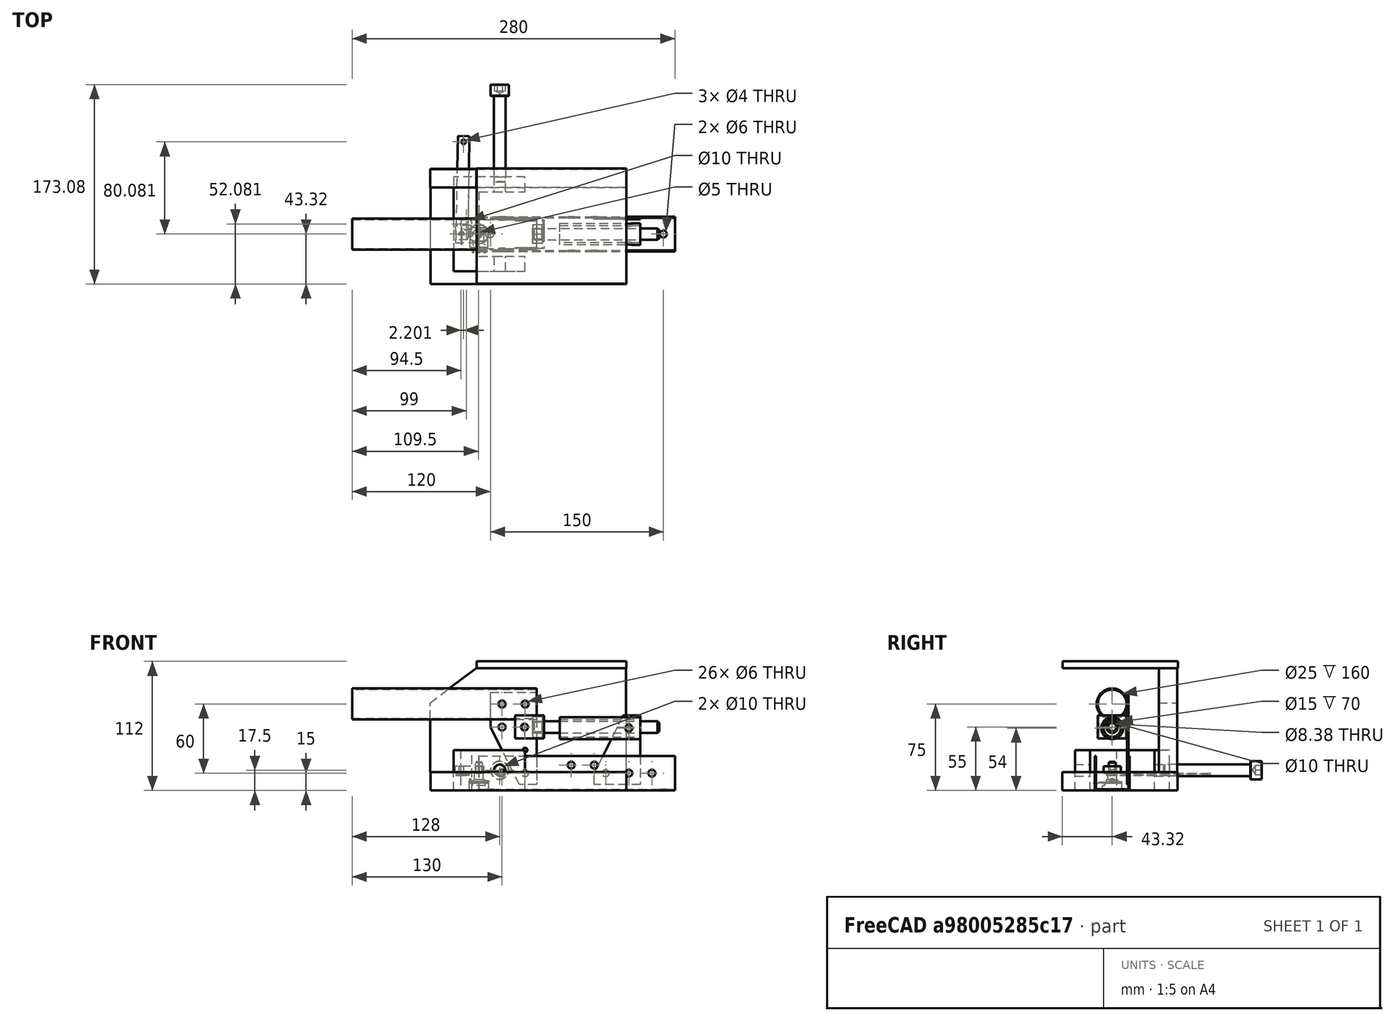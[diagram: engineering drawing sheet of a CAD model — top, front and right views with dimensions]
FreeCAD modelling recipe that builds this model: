
FCSTD DOCUMENT  (FreeCAD 0.19R24267 +99 (Git))
Label: HandBrake
License: All rights reserved
LicenseURL: http://en.wikipedia.org/wiki/All_rights_reserved
objects: TechDraw::DrawViewDimension×36, Sketcher::SketchObject×20, PartDesign::Pad×12, PartDesign::Body×12, TechDraw::DrawProjGroupItem×12, TechDraw::DrawProjGroup×9, PartDesign::Pocket×8, App::Part×7, Part::FeaturePython×3, Part::Mirroring×3, PartDesign::Thickness×2, PartDesign::Chamfer×2, Part::Feature×2, TechDraw::DrawSVGTemplate×2, TechDraw::DrawPage×2, App::DocumentObjectGroup×1
note: 88 computed .brp shape members not serialized (recipe doc carries the construction recipe); baked Part::Feature solids carry a one-line shape summary decoded from their .brp

FEATURE [Sketcher::SketchObject] Sketch
  FullyConstrained = false
  MapMode = 5
  Placement = pos=(0,0,0) rot=(0.57735,0.57735,0.57735;2.0944rad)
  Support = -> [YZ_Plane001]
  sketch-geometry (11):
    g0: LineSegment StartX=-15 StartY=0 StartZ=0 EndX=15 EndY=0 EndZ=0
    g1: LineSegment StartX=15 StartY=0 StartZ=0 EndX=15 EndY=30 EndZ=0
    g2: LineSegment StartX=15 StartY=30 StartZ=0 EndX=-15 EndY=30 EndZ=0
    g3: LineSegment StartX=-15 StartY=30 StartZ=0 EndX=-15 EndY=0 EndZ=0
    g4: LineSegment StartX=-14 StartY=1 StartZ=0 EndX=14 EndY=1 EndZ=0
    g5: LineSegment StartX=14 StartY=1 StartZ=0 EndX=14 EndY=30 EndZ=0
    g6: LineSegment StartX=14 StartY=30 StartZ=0 EndX=-14 EndY=30 EndZ=0
    g7: LineSegment StartX=-14 StartY=30 StartZ=0 EndX=-14 EndY=1 EndZ=0
    g8: LineSegment StartX=-15 StartY=30 StartZ=0 EndX=-14 EndY=30 EndZ=0
    g9: LineSegment StartX=14 StartY=30 StartZ=0 EndX=15 EndY=30 EndZ=0
    g10: LineSegment StartX=5.44004 StartY=1 StartZ=0 EndX=5.44004 EndY=0 EndZ=0
  constraints (30):
    c: Coincident(g0,g1)
    c: Coincident(g1,g2)
    c: Coincident(g2,g3)
    c: Coincident(g3,g0)
    c: Horizontal(g0)
    c: Horizontal(g2)
    c: Vertical(g1)
    c: Vertical(g3)
    c: Coincident(g4,g5)
    c: Coincident(g5,g6)
    c: Coincident(g6,g7)
    c: Coincident(g7,g4)
    c: Horizontal(g4)
    c: Horizontal(g6)
    c: Vertical(g5)
    c: Vertical(g7)
    c: PointOnObject(g5,g2)
    c: Coincident(g8,g3)
    c: Coincident(g8,g7)
    c: Coincident(g9,g5)
    c: Coincident(g9,g1)
    c: DistanceY(g1,g1) = 30
    c: DistanceX(g0,g0) = 30
    c: Equal(g8,g9)
    c: DistanceX(g8,g8) = 1
    c: PointOnObject(g10,g4)
    c: PointOnObject(g10,g0)
    c: Equal(g10,g9)
    c: Perpendicular(g0,g10)
    c: Symmetric(g0,g0,g-1)
FEATURE [PartDesign::Pad] Pad
  Direction = (1,1,1)
  Length = 170
  Length2 = 100
  Placement = pos=(0,0,0) rot=(0.57735,0.57735,0.57735;2.0944rad)
  Profile = -> Sketch
  Type = 0
FEATURE [Sketcher::SketchObject] Sketch001
  FullyConstrained = true
  MapMode = 5
  Support = -> [XY_Plane002]
  sketch-geometry (1):
    g0: Circle CenterX=0 CenterY=0 CenterZ=0 NormalX=0 NormalY=0 NormalZ=1 AngleXU=0 Radius=12.5
  constraints (2):
    c: Coincident(g0,g-1)
    c: Diameter(g0) = 25
FEATURE [PartDesign::Pad] Pad001
  Direction = (1,1,1)
  Length = 160
  Length2 = 100
  Profile = -> Sketch001
  Type = 0
FEATURE [PartDesign::Thickness] Thickness
  Base = -> Pad001 [Face3,Face2]
  BaseFeature = -> Pad001
  Intersection = false
  Join = 1
  Mode = 1
  SupportTransform = false
  Value = 1
FEATURE [Sketcher::SketchObject] Sketch002
  ExternalGeometry = -> [Thickness]
  FullyConstrained = true
  MapMode = 5
  Placement = pos=(0,0,0) rot=(1,0,0;1.5708rad)
  Support = -> [XZ_Plane002]
  sketch-geometry (2):
    g0: Circle CenterX=0 CenterY=10 CenterZ=0 NormalX=0 NormalY=0 NormalZ=1 AngleXU=0 Radius=3
    g1: Circle CenterX=0 CenterY=30 CenterZ=0 NormalX=0 NormalY=0 NormalZ=1 AngleXU=0 Radius=3
  constraints (6):
    c: PointOnObject(g0,g-2)
    c: Diameter(g0) = 6
    c: PointOnObject(g1,g-2)
    c: Equal(g1,g0)
    c: Distance(g1,g0) = 20
    c: DistanceY(g-1,g0) = 10
FEATURE [PartDesign::Pocket] Pocket
  BaseFeature = -> Thickness
  Length = 5
  Length2 = 100
  Midplane = true
  Profile = -> Sketch002
  Type = 1
FEATURE [PartDesign::Body] Body001  label="Рычаг"
  Group = -> [Sketch001,Pad001,Thickness,Sketch002,Pocket]
  Origin = -> Origin002
  Placement = pos=(50,0,75) rot=(0,-1,0;1.5708rad)
  Tip = -> Pocket
FEATURE [Sketcher::SketchObject] Sketch003
  ExternalGeometry = -> [Pad]
  FullyConstrained = false
  MapMode = 5
  Placement = pos=(-6.6e-15,-15,3.3e-15) rot=(-0.57735,-0.57735,0.57735;4.18879rad)
  Support = -> [Pad]
  sketch-geometry (7):
    g0: Circle CenterX=-15 CenterY=20 CenterZ=0 NormalX=0 NormalY=0 NormalZ=1 AngleXU=0 Radius=3
    g1: Circle CenterX=-15 CenterY=150 CenterZ=0 NormalX=0 NormalY=0 NormalZ=1 AngleXU=0 Radius=3
    g2: LineSegment StartX=-15 StartY=170 StartZ=0 EndX=-15 EndY=0 EndZ=0
    g3: Circle CenterX=-15 CenterY=130 CenterZ=0 NormalX=0 NormalY=0 NormalZ=1 AngleXU=0 Radius=3
    g4: LineSegment StartX=-22 StartY=170 StartZ=0 EndX=-22 EndY=0 EndZ=0
    g5: Circle CenterX=-22 CenterY=100 CenterZ=0 NormalX=0 NormalY=0 NormalZ=1 AngleXU=0 Radius=3
    g6: Circle CenterX=-22 CenterY=80 CenterZ=0 NormalX=0 NormalY=0 NormalZ=1 AngleXU=0 Radius=3
  constraints (23):
    c: Equal(g1,g0)
    c: Diameter(g0) = 6
    c: PointOnObject(g2,g-4)
    c: Vertical(g2)
    c: Distance(g-4) = 30
    c: Distance(g2,g-5) = 15
    c: PointOnObject(g1,g2)
    c: PointOnObject(g0,g2)
    c: Distance(g0,g2) = 20
    c: Distance(g1,g2) = 20
    c: PointOnObject(g3,g2)
    c: Equal(g3,g1)
    c: Distance(g3,g1) = 20
    c: PointOnObject(g4,g-4)
    c: Vertical(g4)
    c: DistanceX(g-4,g4) = 8
    c: PointOnObject(g5,g4)
    c: Diameter(g5) = 6
    c: DistanceY(g4,g5) = 100
    c: PointOnObject(g6,g4)
    c: Equal(g6,g5)
    c: DistanceY(g6,g5) = 20
    c: PointOnObject(g4,g-1)
FEATURE [PartDesign::Pocket] Pocket001
  BaseFeature = -> Pad
  Length = 5
  Length2 = 100
  Placement = pos=(0,0,0) rot=(0.57735,0.57735,0.57735;2.0944rad)
  Profile = -> Sketch003
  Type = 1
FEATURE [Sketcher::SketchObject] Sketch004
  FullyConstrained = true
  MapMode = 5
  Placement = pos=(0,0,0) rot=(1,0,0;1.5708rad)
  Support = -> [XZ_Plane004]
  sketch-geometry (15):
    g0: LineSegment StartX=-20 StartY=40 StartZ=0 EndX=20 EndY=40 EndZ=0
    g1: LineSegment StartX=20 StartY=40 StartZ=0 EndX=20 EndY=-40 EndZ=0
    g2: LineSegment StartX=20 StartY=-40 StartZ=0 EndX=-20 EndY=-40 EndZ=0
    g3: LineSegment StartX=-20 StartY=-40 StartZ=0 EndX=-20 EndY=40 EndZ=0
    g4: Circle CenterX=-10 CenterY=30 CenterZ=0 NormalX=0 NormalY=0 NormalZ=1 AngleXU=0 Radius=3
    g5: Circle CenterX=10 CenterY=30 CenterZ=0 NormalX=0 NormalY=0 NormalZ=1 AngleXU=0 Radius=3
    g6: LineSegment StartX=-10 StartY=30 StartZ=0 EndX=10 EndY=30 EndZ=0
    g7: LineSegment StartX=10 StartY=30 StartZ=0 EndX=10 EndY=-30 EndZ=0
    g8: LineSegment StartX=10 StartY=-30 StartZ=0 EndX=-10 EndY=-30 EndZ=0
    g9: LineSegment StartX=-10 StartY=-30 StartZ=0 EndX=-10 EndY=30 EndZ=0
    g10: Circle CenterX=10 CenterY=-30 CenterZ=0 NormalX=0 NormalY=0 NormalZ=1 AngleXU=0 Radius=3
    g11: Circle CenterX=-10 CenterY=-30 CenterZ=0 NormalX=0 NormalY=0 NormalZ=1 AngleXU=0 Radius=3
    g12: Circle CenterX=-10 CenterY=10 CenterZ=0 NormalX=0 NormalY=0 NormalZ=1 AngleXU=0 Radius=3
    g13: Circle CenterX=10 CenterY=10 CenterZ=0 NormalX=0 NormalY=0 NormalZ=1 AngleXU=0 Radius=3
    g14: Circle CenterX=10 CenterY=-10 CenterZ=0 NormalX=0 NormalY=0 NormalZ=1 AngleXU=0 Radius=2
  constraints (40):
    c: Coincident(g0,g1)
    c: Coincident(g1,g2)
    c: Coincident(g2,g3)
    c: Coincident(g3,g0)
    c: Horizontal(g0)
    c: Horizontal(g2)
    c: Vertical(g1)
    c: Vertical(g3)
    c: Diameter(g4) = 6
    c: Equal(g4,g5)
    c: Coincident(g6,g7)
    c: Coincident(g7,g8)
    c: Coincident(g8,g9)
    c: Coincident(g9,g6)
    c: Horizontal(g6)
    c: Horizontal(g8)
    c: Vertical(g7)
    c: Vertical(g9)
    c: Coincident(g6,g4)
    c: Coincident(g6,g5)
    c: DistanceX(g6,g6) = 20
    c: DistanceY(g7,g7) = 60
    c: Coincident(g10,g7)
    c: Coincident(g11,g8)
    c: Equal(g10,g5)
    c: Equal(g5,g11)
    c: PointOnObject(g12,g9)
    c: Equal(g12,g4)
    c: DistanceY(g12,g4) = 20
    c: DistanceY(g4,g0) = 10
    c: DistanceX(g0,g4) = 10
    c: DistanceX(g5,g0) = 10
    c: DistanceY(g1,g10) = 10
    c: Symmetric(g5,g11,g-1)
    c: PointOnObject(g13,g7)
    c: Equal(g13,g12)
    c: Distance(g13,g5) = 20
    c: PointOnObject(g14,g7)
    c: Distance(g14,g13) = 20
    c: Diameter(g14) = 4
FEATURE [PartDesign::Pad] Pad002
  Direction = (1,1,1)
  Length = 1
  Length2 = 100
  Placement = pos=(0,0,0) rot=(1,0,0;1.5708rad)
  Profile = -> Sketch004
  Type = 0
FEATURE [Sketcher::SketchObject] Sketch005
  FullyConstrained = false
  MapMode = 5
  Placement = pos=(0,0,0) rot=(1,0,0;1.5708rad)
  Support = -> [XZ_Plane005]
  sketch-geometry (12):
    g0: LineSegment StartX=-20 StartY=30 StartZ=0 EndX=20 EndY=30 EndZ=0
    g1: LineSegment StartX=20 StartY=30 StartZ=0 EndX=20 EndY=-30 EndZ=0
    g2: LineSegment StartX=20 StartY=-30 StartZ=0 EndX=-20 EndY=-30 EndZ=0
    g3: LineSegment StartX=-20 StartY=-30 StartZ=0 EndX=-20 EndY=30 EndZ=0
    g4: Circle CenterX=-10 CenterY=20 CenterZ=0 NormalX=0 NormalY=0 NormalZ=1 AngleXU=0 Radius=3
    g5: Circle CenterX=10 CenterY=20 CenterZ=0 NormalX=0 NormalY=0 NormalZ=1 AngleXU=0 Radius=3
    g6: LineSegment StartX=-10 StartY=20 StartZ=0 EndX=10 EndY=20 EndZ=0
    g7: LineSegment StartX=10 StartY=20 StartZ=0 EndX=10 EndY=-20 EndZ=0
    g8: LineSegment StartX=10 StartY=-20 StartZ=0 EndX=-10 EndY=-20 EndZ=0
    g9: LineSegment StartX=-10 StartY=-20 StartZ=0 EndX=-10 EndY=20 EndZ=0
    g10: Circle CenterX=10 CenterY=-20 CenterZ=0 NormalX=0 NormalY=0 NormalZ=1 AngleXU=0 Radius=3
    g11: Circle CenterX=-10 CenterY=-20 CenterZ=0 NormalX=0 NormalY=0 NormalZ=1 AngleXU=0 Radius=3
  constraints (30):
    c: Coincident(g0,g1)
    c: Coincident(g1,g2)
    c: Coincident(g2,g3)
    c: Coincident(g3,g0)
    c: Horizontal(g0)
    c: Horizontal(g2)
    c: Vertical(g1)
    c: Vertical(g3)
    c: Diameter(g4) = 6
    c: Equal(g4,g5)
    c: Coincident(g6,g7)
    c: Coincident(g7,g8)
    c: Coincident(g8,g9)
    c: Coincident(g9,g6)
    c: Horizontal(g6)
    c: Horizontal(g8)
    c: Vertical(g9)
    c: Coincident(g6,g4)
    c: Coincident(g6,g5)
    c: DistanceX(g6,g6) = 20
    c: DistanceY(g7,g7) = 40
    c: Coincident(g10,g7)
    c: Coincident(g11,g8)
    c: Equal(g10,g5)
    c: Equal(g5,g11)
    c: DistanceY(g4,g0) = 10
    c: DistanceX(g0,g4) = 10
    c: DistanceX(g5,g0) = 10
    c: DistanceY(g1,g10) = 10
    c: Symmetric(g5,g11,g-1)
FEATURE [PartDesign::Pad] Pad003
  Direction = (1,1,1)
  Length = 1
  Length2 = 100
  Placement = pos=(0,0,0) rot=(1,0,0;1.5708rad)
  Profile = -> Sketch005
  Type = 0
FEATURE [Sketcher::SketchObject] Sketch008
  FullyConstrained = true
  MapMode = 5
  Support = -> [XY_Plane016]
  sketch-geometry (12):
    g0: LineSegment StartX=-12.5 StartY=12.5 StartZ=0 EndX=12.5 EndY=12.5 EndZ=0
    g1: LineSegment StartX=12.5 StartY=12.5 StartZ=0 EndX=12.5 EndY=-12.5 EndZ=0
    g2: LineSegment StartX=12.5 StartY=-12.5 StartZ=0 EndX=-12.5 EndY=-12.5 EndZ=0
    g3: LineSegment StartX=-12.5 StartY=-12.5 StartZ=0 EndX=-12.5 EndY=12.5 EndZ=0
    g4: LineSegment StartX=-11.5 StartY=11.5 StartZ=0 EndX=11.5 EndY=11.5 EndZ=0
    g5: LineSegment StartX=11.5 StartY=11.5 StartZ=0 EndX=11.5 EndY=-11.5 EndZ=0
    g6: LineSegment StartX=11.5 StartY=-11.5 StartZ=0 EndX=-11.5 EndY=-11.5 EndZ=0
    g7: LineSegment StartX=-11.5 StartY=-11.5 StartZ=0 EndX=-11.5 EndY=11.5 EndZ=0
    g8: LineSegment StartX=-11.5 StartY=12.5 StartZ=0 EndX=-11.5 EndY=-11.5 EndZ=0
    g9: LineSegment StartX=11.5 StartY=12.5 StartZ=0 EndX=11.5 EndY=-11.5 EndZ=0
    g10: LineSegment StartX=-12.5 StartY=12.5 StartZ=0 EndX=-11.5 EndY=12.5 EndZ=0
    g11: LineSegment StartX=11.5 StartY=12.5 StartZ=0 EndX=12.5 EndY=12.5 EndZ=0
  constraints (32):
    c: Coincident(g0,g1)
    c: Coincident(g1,g2)
    c: Coincident(g2,g3)
    c: Coincident(g3,g0)
    c: Horizontal(g0)
    c: Horizontal(g2)
    c: Vertical(g1)
    c: Vertical(g3)
    c: Symmetric(g0,g2,g-1)
    c: DistanceY(g3,g3) = 25
    c: DistanceX(g2,g2) = 25
    c: Coincident(g4,g5)
    c: Coincident(g5,g6)
    c: Coincident(g6,g7)
    c: Coincident(g7,g4)
    c: Horizontal(g4)
    c: Horizontal(g6)
    c: Vertical(g5)
    c: Vertical(g7)
    c: DistanceY(g4,g3) = 1
    c: DistanceX(g3,g4) = 1
    c: Symmetric(g4,g6,g-1)
    c: PointOnObject(g8,g0)
    c: Coincident(g8,g6)
    c: Vertical(g8)
    c: PointOnObject(g9,g0)
    c: Coincident(g9,g5)
    c: Vertical(g9)
    c: Coincident(g10,g3)
    c: Coincident(g10,g8)
    c: Coincident(g11,g9)
    c: Coincident(g11,g1)
FEATURE [PartDesign::Pad] Pad004
  Direction = (1,1,1)
  Length = 20
  Length2 = 100
  Profile = -> Sketch008
  Type = 0
FEATURE [Sketcher::SketchObject] Sketch009
  ExternalGeometry = -> [Pad004]
  FullyConstrained = false
  MapMode = 5
  Placement = pos=(12.5,0,0) rot=(0.57735,0.57735,0.57735;2.0944rad)
  Support = -> [Pad004]
  sketch-geometry (1):
    g0: Circle CenterX=4.5 CenterY=10 CenterZ=0 NormalX=0 NormalY=0 NormalZ=1 AngleXU=0 Radius=3
  constraints (2):
    c: Diameter(g0) = 6
    c: DistanceX(g0,g-5) = 8
FEATURE [PartDesign::Pocket] Pocket003
  BaseFeature = -> Pad004
  Length = 5
  Length2 = 100
  Profile = -> Sketch009
  Type = 1
FEATURE [Sketcher::SketchObject] Sketch010
  ExternalGeometry = -> [Pocket003]
  FullyConstrained = true
  MapMode = 5
  Placement = pos=(0,-12.5,0) rot=(1,0,0;1.5708rad)
  Support = -> [Pocket003]
  sketch-geometry (1):
    g0: Circle CenterX=-6e-16 CenterY=10 CenterZ=0 NormalX=0 NormalY=0 NormalZ=1 AngleXU=0 Radius=5
  constraints (2):
    c: Symmetric(g-5,g-6,g0)
    c: Diameter(g0) = 10
FEATURE [PartDesign::Pocket] Pocket004
  BaseFeature = -> Pocket003
  Length = 5
  Length2 = 100
  Profile = -> Sketch010
  Type = 1
FEATURE [PartDesign::Body] _______________________004  label="Крепление пружины"
  Group = -> [Sketch008,Pad004,Sketch009,Pocket003,Sketch010,Pocket004]
  Origin = -> Origin016
  Placement = pos=(44,1e-14,45) rot=(0,0,1;1.5708rad)
  Tip = -> Pocket004
FEATURE [Sketcher::SketchObject] Sketch007
  FullyConstrained = true
  MapMode = 5
  Support = -> [XY_Plane015]
  sketch-geometry (1):
    g0: Circle CenterX=0 CenterY=0 CenterZ=0 NormalX=0 NormalY=0 NormalZ=1 AngleXU=0 Radius=7.5
  constraints (2):
    c: Coincident(g0,g-1)
    c: Diameter(g0) = 15
FEATURE [PartDesign::Pad] Pad005
  Direction = (1,1,1)
  Length = 70
  Length2 = 100
  Profile = -> Sketch007
  Type = 0
FEATURE [PartDesign::Thickness] Thickness001
  Base = -> Pad005 [Face3,Face2]
  BaseFeature = -> Pad005
  Intersection = false
  Join = 0
  Mode = 0
  SupportTransform = false
  Value = 2
FEATURE [Sketcher::SketchObject] Sketch011
  FullyConstrained = true
  MapMode = 5
  Placement = pos=(0,0,0) rot=(0.57735,0.57735,0.57735;2.0944rad)
  Support = -> [YZ_Plane015]
  sketch-geometry (1):
    g0: Circle CenterX=0 CenterY=10 CenterZ=0 NormalX=0 NormalY=0 NormalZ=1 AngleXU=0 Radius=3
  constraints (3):
    c: PointOnObject(g0,g-2)
    c: Diameter(g0) = 6
    c: DistanceY(g-1,g0) = 10
FEATURE [PartDesign::Pocket] Pocket005
  BaseFeature = -> Thickness001
  Length = 5
  Length2 = 100
  Midplane = true
  Profile = -> Sketch011
  Reversed = true
  Type = 1
FEATURE [PartDesign::Body] Body004  label="Втулка упор пружины"
  Group = -> [Sketch007,Pad005,Thickness001,Sketch011,Pocket005]
  Origin = -> Origin015
  Placement = pos=(140,-2e-15,54) rot=(0.57735,-0.57735,-0.57735;2.0944rad)
  Tip = -> Pocket005
FEATURE [Part::FeaturePython] ThreadedRod  label="M10x110.0-ThreadedRod"  # Fasteners workbench fastener (typed FeaturePython)
  Placement = pos=(46.5,1e-14,55) rot=(0,-1,0;1.5708rad)
  baseObject = -> _______________________004 [Edge27]
  diameter = 10
  diameterCustom = 6
  invert = true
  length = 110
  matchOuter = false
  offset = 10
  pitchCustom = 1
  thread = false
FEATURE [PartDesign::Chamfer] Chamfer
  Angle = 45
  Base = -> Pad003 [Edge1]
  BaseFeature = -> Pad003
  ChamferType = 1
  FlipDirection = false
  Placement = pos=(0,0,0) rot=(1,0,0;1.5708rad)
  Size = 25
  Size2 = 50
  SupportTransform = false
FEATURE [PartDesign::Body] Body003  label="Пластина001"
  Group = -> [Sketch005,Pad003,Chamfer]
  Origin = -> Origin005
  Placement = pos=(120,-13,35) rot=(0,0,1;0rad)
  Tip = -> Chamfer
FEATURE [PartDesign::Chamfer] Chamfer001
  Angle = 45
  Base = -> Pad002 [Edge8]
  BaseFeature = -> Pad002
  ChamferType = 1
  FlipDirection = false
  Placement = pos=(0,0,0) rot=(1,0,0;1.5708rad)
  Size = 25
  Size2 = 50
  SupportTransform = false
FEATURE [PartDesign::Body] Body002  label="Пластина"
  Group = -> [Sketch004,Pad002,Chamfer001]
  Origin = -> Origin004
  Placement = pos=(30,-13,45) rot=(0,0,1;0rad)
  Tip = -> Chamfer001
FEATURE [Part::FeaturePython] Nut  label="M10-Nut"  # Fasteners workbench fastener (typed FeaturePython)
  Placement = pos=(55,1.2e-14,55) rot=(0,-1,0;1.5708rad)
  baseObject = -> ThreadedRod [Edge2]
  diameter = 10
  invert = false
  matchOuter = false
  offset = -7
  thread = false
  type = 7
FEATURE [Part::Mirroring] mirror  label="Пластина (mirrored)"
  Base = (-9e-16,0,1)
  Normal = (-7e-16,-1,0)
  Source = -> Body002
FEATURE [App::Part] Part001  label="Рычаг001"
  Group = -> [Body001,Body002,_______________________004,ThreadedRod,Nut,mirror]
  Origin = -> Origin003
  Placement = pos=(-20,0,0) rot=(0,0,1;0rad)
FEATURE [Part::Mirroring] mirror001  label="Пластина001 (mirrored)"
  Base = (-9e-16,0,1)
  Normal = (-7e-16,-1,0)
  Source = -> Body003
FEATURE [App::Part] Part003  label="Крепление"
  Group = -> [Body003,Body004,mirror001]
  Origin = -> Origin017
  Placement = pos=(20,0,0) rot=(0,0,1;0rad)
FEATURE [Part::Feature] Part__Feature202  label="COMPOUND"
  shape: bbox 8.7 x 5.6 x 10.5 mm, 0 faces, 0 solids (baked)
FEATURE [Part::Feature] Part__Feature203  label="COMPOUND001"
  shape: bbox 17.4 x 24.95 x 24.8 mm, 138 faces, 12 solids (baked)
FEATURE [Sketcher::SketchObject] Sketch035
  FullyConstrained = true
  MapMode = 5
  Support = -> [XY_Plane029]
  sketch-geometry (6):
    g0: LineSegment StartX=-7.5 StartY=-12.5 StartZ=0 EndX=7.5 EndY=-12.5 EndZ=0
    g1: LineSegment StartX=7.5 StartY=-12.5 StartZ=0 EndX=7.5 EndY=12.5 EndZ=0
    g2: LineSegment StartX=7.5 StartY=12.5 StartZ=0 EndX=-7.5 EndY=12.5 EndZ=0
    g3: LineSegment StartX=-7.5 StartY=12.5 StartZ=0 EndX=-7.5 EndY=-12.5 EndZ=0
    g4: Circle CenterX=0 CenterY=-7.5 CenterZ=0 NormalX=0 NormalY=0 NormalZ=1 AngleXU=0 Radius=2.5
    g5: Circle CenterX=0 CenterY=7.5 CenterZ=0 NormalX=0 NormalY=0 NormalZ=1 AngleXU=0 Radius=2
  constraints (17):
    c: Coincident(g0,g1)
    c: Coincident(g1,g2)
    c: Coincident(g2,g3)
    c: Coincident(g3,g0)
    c: Horizontal(g0)
    c: Horizontal(g2)
    c: Vertical(g1)
    c: Vertical(g3)
    c: Symmetric(g1,g0,g-1)
    c: DistanceX(g2,g2) = 15
    c: DistanceY(g3,g3) = 25
    c: PointOnObject(g4,g-2)
    c: Diameter(g4) = 5
    c: DistanceY(g0,g4) = 5
    c: PointOnObject(g5,g-2)
    c: Diameter(g5) = 4
    c: DistanceY(g5,g2) = 5
FEATURE [PartDesign::Pad] Pad012
  Direction = (1,1,1)
  Length = 6
  Length2 = 100
  Profile = -> Sketch035
  Type = 0
FEATURE [PartDesign::Body] Body005  label="Рычаг потенциометра"
  Group = -> [Sketch035,Pad012]
  Origin = -> Origin029
  Placement = pos=(-8,-2e-15,15) rot=(0,0,1;1.5708rad)
  Tip = -> Pad012
FEATURE [Sketcher::SketchObject] Sketch036
  FullyConstrained = true
  MapMode = 5
  Support = -> [XY_Plane030]
  sketch-geometry (6):
    g0: LineSegment StartX=-5 StartY=45 StartZ=0 EndX=5 EndY=45 EndZ=0
    g1: LineSegment StartX=5 StartY=45 StartZ=0 EndX=5 EndY=-45 EndZ=0
    g2: LineSegment StartX=5 StartY=-45 StartZ=0 EndX=-5 EndY=-45 EndZ=0
    g3: LineSegment StartX=-5 StartY=-45 StartZ=0 EndX=-5 EndY=45 EndZ=0
    g4: Circle CenterX=0 CenterY=40 CenterZ=0 NormalX=0 NormalY=0 NormalZ=1 AngleXU=0 Radius=2
    g5: Circle CenterX=0 CenterY=-40 CenterZ=0 NormalX=0 NormalY=0 NormalZ=1 AngleXU=0 Radius=2
  constraints (17):
    c: Coincident(g0,g1)
    c: Coincident(g1,g2)
    c: Coincident(g2,g3)
    c: Coincident(g3,g0)
    c: Horizontal(g0)
    c: Horizontal(g2)
    c: Vertical(g1)
    c: Vertical(g3)
    c: Symmetric(g0,g2,g-1)
    c: PointOnObject(g4,g-2)
    c: PointOnObject(g5,g-2)
    c: Equal(g5,g4)
    c: Diameter(g4) = 4
    c: DistanceY(g4,g0) = 5
    c: DistanceY(g2,g5) = 5
    c: DistanceY(g1,g1) = 90
    c: DistanceX(g0,g0) = 10
FEATURE [PartDesign::Pad] Pad013
  Direction = (1,1,1)
  Length = 1.5
  Length2 = 100
  Profile = -> Sketch036
  Type = 0
FEATURE [PartDesign::Body] Body006  label="Штанга потенциометра"
  Group = -> [Sketch036,Pad013]
  Origin = -> Origin030
  Placement = pos=(-13.9974,40.0872,13) rot=(0,0,-1;0.017453rad)
  Tip = -> Pad013
FEATURE [App::Part] Document  label="Потенциометр"
  Group = -> [Part__Feature202,Part__Feature203,Body005,Body006]
  Origin = -> Origin028
  Placement = pos=(100,-24,22) rot=(0.57735,-0.57735,-0.57735;4.18879rad)
FEATURE [Sketcher::SketchObject] Sketch037
  ExternalGeometry = -> [Pocket001]
  FullyConstrained = true
  MapMode = 5
  Placement = pos=(0,0,1e-16) rot=(0.707107,0.707107,0;3.14159rad)
  Support = -> [Pocket001]
  sketch-geometry (2):
    g0: Circle CenterX=0 CenterY=160 CenterZ=0 NormalX=0 NormalY=0 NormalZ=1 AngleXU=0 Radius=3
    g1: Circle CenterX=0 CenterY=10 CenterZ=0 NormalX=0 NormalY=0 NormalZ=1 AngleXU=0 Radius=3
  constraints (6):
    c: PointOnObject(g0,g-2)
    c: PointOnObject(g1,g-2)
    c: Equal(g1,g0)
    c: Diameter(g1) = 6
    c: DistanceY(g-1,g1) = 10
    c: DistanceY(g0,g-5) = 10
FEATURE [PartDesign::Pocket] Pocket006
  BaseFeature = -> Pocket001
  Length = 5
  Length2 = 100
  Placement = pos=(0,0,0) rot=(0.57735,0.57735,0.57735;2.0944rad)
  Profile = -> Sketch037
  Type = 0
FEATURE [PartDesign::Body] Body  label="Основание"
  Group = -> [Sketch,Pad,Sketch003,Pocket001,Sketch037,Pocket006]
  Origin = -> Origin001
  Tip = -> Pocket006
FEATURE [App::Part] Part002  label="Основание001"
  Group = -> [Body,Part003,Document]
  Origin = -> Origin006
FEATURE [Sketcher::SketchObject] Sketch038
  FullyConstrained = false
  MapMode = 5
  Support = -> [XY_Plane031]
  sketch-geometry (4):
    g0: LineSegment StartX=-42.0434 StartY=56.6762 StartZ=0 EndX=127.957 EndY=56.6762 EndZ=0
    g1: LineSegment StartX=127.957 StartY=56.6762 StartZ=0 EndX=127.957 EndY=-43.3238 EndZ=0
    g2: LineSegment StartX=127.957 StartY=-43.3238 StartZ=0 EndX=-42.0434 EndY=-43.3238 EndZ=0
    g3: LineSegment StartX=-42.0434 StartY=-43.3238 StartZ=0 EndX=-42.0434 EndY=56.6762 EndZ=0
  constraints (10):
    c: Coincident(g0,g1)
    c: Coincident(g1,g2)
    c: Coincident(g2,g3)
    c: Coincident(g3,g0)
    c: Horizontal(g0)
    c: Horizontal(g2)
    c: Vertical(g1)
    c: Vertical(g3)
    c: DistanceY(g1,g1) = 100
    c: DistanceX(g0,g0) = 170
FEATURE [PartDesign::Pad] Pad014
  Direction = (1,1,1)
  Length = 16
  Length2 = 100
  Profile = -> Sketch038
  Type = 0
FEATURE [PartDesign::Body] Body007  label="Короб основа"
  Group = -> [Sketch038,Pad014]
  Origin = -> Origin031
  Tip = -> Pad014
FEATURE [Sketcher::SketchObject] Sketch044
  FullyConstrained = false
  MapMode = 5
  Support = -> [XY_Plane048]
  sketch-geometry (8):
    g0: LineSegment StartX=0 StartY=36.7604 StartZ=0 EndX=40 EndY=36.7604 EndZ=0
    g1: LineSegment StartX=0 StartY=36.7604 StartZ=0 EndX=0 EndY=-19.2396 EndZ=0
    g2: LineSegment StartX=0 StartY=-19.2396 StartZ=0 EndX=40 EndY=-19.2396 EndZ=0
    g3: LineSegment StartX=40 StartY=36.7604 StartZ=0 EndX=40 EndY=49.7604 EndZ=0
    g4: LineSegment StartX=40 StartY=49.7604 StartZ=0 EndX=-22 EndY=49.7604 EndZ=0
    g5: LineSegment StartX=-22 StartY=49.7604 StartZ=0 EndX=-22 EndY=-32.2395 EndZ=0
    g6: LineSegment StartX=-22 StartY=-32.2395 StartZ=0 EndX=39.9696 EndY=-32.2395 EndZ=0
    g7: LineSegment StartX=39.9696 StartY=-32.2395 StartZ=0 EndX=40 EndY=-19.2396 EndZ=0
  constraints (22):
    c: PointOnObject(g0,g-2)
    c: Horizontal(g0)
    c: Coincident(g1,g0)
    c: PointOnObject(g1,g-2)
    c: Coincident(g2,g1)
    c: Horizontal(g2)
    c: Coincident(g3,g0)
    c: Vertical(g3)
    c: Coincident(g4,g3)
    c: Horizontal(g4)
    c: Coincident(g5,g4)
    c: Vertical(g5)
    c: Coincident(g6,g5)
    c: Horizontal(g6)
    c: Coincident(g7,g6)
    c: Coincident(g7,g2)
    c: DistanceX(g0,g0) = 40
    c: Equal(g0,g2)
    c: DistanceY(g1,g1) = 56
    c: DistanceY(g3,g3) = 13
    c: Equal(g3,g7)
    c: DistanceX(g5,g1) = 22
FEATURE [Part::FeaturePython] Screw004  label="M10x75-Screw"  # Fasteners workbench fastener (typed FeaturePython)
  Placement = pos=(18,119.76,17.5) rot=(-1,0,0;1.5708rad)
  baseObject = -> Pocket031 [Edge24]
  diameter = 9
  invert = false
  length = 12
  lengthCustom = 75
  matchOuter = false
  offset = 70
  thread = false
  type = 34
FEATURE [PartDesign::Pad] Pad022
  Direction = (1,1,1)
  Length = 35
  Length2 = 100
  Profile = -> Sketch044
  Type = 0
FEATURE [Sketcher::SketchObject] Sketch047
  ExternalGeometry = -> [Pad022]
  FullyConstrained = true
  MapMode = 5
  Placement = pos=(0,49.7604,0) rot=(0,0.707107,0.707107;3.14159rad)
  Support = -> [Pad022]
  sketch-geometry (2):
    g0: LineSegment StartX=-18 StartY=35 StartZ=0 EndX=-18 EndY=0 EndZ=0
    g1: Circle CenterX=-18 CenterY=17.5 CenterZ=0 NormalX=0 NormalY=0 NormalZ=1 AngleXU=0 Radius=5
  constraints (8):
    c: PointOnObject(g0,g-4)
    c: PointOnObject(g0,g-6)
    c: Vertical(g0)
    c: DistanceX(g-5,g0) = 22
    c: PointOnObject(g1,g0)
    c: Diameter(g1) = 10
    c: DistanceY(g-5,g-5) = 35
    c: DistanceY(g1,g0) = 17.5
FEATURE [PartDesign::Pocket] Pocket030
  BaseFeature = -> Pad022
  Length = 5
  Length2 = 100
  Profile = -> Sketch047
  Type = 1
FEATURE [Sketcher::SketchObject] Sketch048
  ExternalGeometry = -> [Pocket030]
  FullyConstrained = true
  MapMode = 5
  Placement = pos=(0,0,0) rot=(1,0,0;3.14159rad)
  Support = -> [Pocket030]
  sketch-geometry (1):
    g0: Circle CenterX=-11 CenterY=-8.76048 CenterZ=0 NormalX=0 NormalY=0 NormalZ=1 AngleXU=0 Radius=5
  constraints (5):
    c: Diameter(g0) = 10
    c: Distance(g-4) = 82
    c: DistanceX(g-4,g-5) = 22
    c: DistanceX(g-6,g0) = 11
    c: DistanceY(g0,g-4) = 41
FEATURE [PartDesign::Pocket] Pocket031
  BaseFeature = -> Pocket030
  Length = 5
  Length2 = 100
  Profile = -> Sketch048
  Type = 1
FEATURE [PartDesign::Body] Body020  label="струбцина"
  Group = -> [Sketch044,Pad022,Sketch047,Pocket030,Sketch048,Pocket031]
  Origin = -> Origin047
  Tip = -> Pocket031
FEATURE [App::Part] Part027  label="Струбцына"
  Group = -> [Body020,Screw004]
  Origin = -> Origin048
  Placement = pos=(26,25,-22) rot=(-0.57735,-0.57735,0.57735;4.18879rad)
FEATURE [Sketcher::SketchObject] Sketch049
  FullyConstrained = false
  MapMode = 5
  Placement = pos=(0,0,0) rot=(1,0,0;1.5708rad)
  Support = -> [XZ_Plane050]
  sketch-geometry (7):
    g0: LineSegment StartX=0 StartY=91.4349 StartZ=0 EndX=90 EndY=91.4349 EndZ=0
    g1: LineSegment StartX=90 StartY=91.4349 StartZ=0 EndX=90 EndY=-78.5651 EndZ=0
    g2: LineSegment StartX=90 StartY=-78.5651 StartZ=0 EndX=0 EndY=-78.5651 EndZ=0
    g3: LineSegment StartX=0 StartY=-78.5651 StartZ=0 EndX=0 EndY=91.4349 EndZ=0
    g4: LineSegment StartX=0 StartY=91.4349 StartZ=0 EndX=60 EndY=91.4349 EndZ=0
    g5: LineSegment StartX=60 StartY=91.4349 StartZ=0 EndX=90 EndY=51.4349 EndZ=0
    g6: LineSegment StartX=90 StartY=51.4349 StartZ=0 EndX=90 EndY=-78.5651 EndZ=0
  constraints (19):
    c: Coincident(g0,g1)
    c: Coincident(g1,g2)
    c: Coincident(g2,g3)
    c: Coincident(g3,g0)
    c: Horizontal(g0)
    c: Horizontal(g2)
    c: Vertical(g1)
    c: Vertical(g3)
    c: PointOnObject(g0,g-2)
    c: DistanceY(g3,g3) = 170
    c: DistanceX(g0,g0) = 90
    c: Coincident(g4,g3)
    c: PointOnObject(g4,g0)
    c: Coincident(g5,g4)
    c: PointOnObject(g5,g1)
    c: Coincident(g6,g5)
    c: Coincident(g6,g2)
    c: DistanceX(g4,g4) = 60
    c: DistanceY(g6,g6) = 130
FEATURE [PartDesign::Pad] Pad023
  Direction = (1,1,1)
  Length = 16
  Length2 = 100
  Placement = pos=(0,0,0) rot=(1,0,0;1.5708rad)
  Profile = -> Sketch049
  Type = 0
FEATURE [PartDesign::Body] Body021  label="Боковина"
  Group = -> [Sketch049,Pad023]
  Origin = -> Origin049
  Placement = pos=(49,-27,16) rot=(0,-1,0;1.5708rad)
  Tip = -> Pad023
FEATURE [Part::Mirroring] mirror002  label="Боковина (mirrored)"
  Base = (-0.0434494,0.676177,-1)
  Normal = (0,-1,0)
  Placement = pos=(0,12,0) rot=(0,0,1;0rad)
  Source = -> Body021
FEATURE [Sketcher::SketchObject] Sketch050
  FullyConstrained = true
  MapMode = 5
  Placement = pos=(0,0,0) rot=(0.57735,0.57735,0.57735;2.0944rad)
  Support = -> [YZ_Plane051]
  sketch-geometry (4):
    g0: LineSegment StartX=-50 StartY=65 StartZ=0 EndX=50 EndY=65 EndZ=0
    g1: LineSegment StartX=50 StartY=65 StartZ=0 EndX=50 EndY=-65 EndZ=0
    g2: LineSegment StartX=50 StartY=-65 StartZ=0 EndX=-50 EndY=-65 EndZ=0
    g3: LineSegment StartX=-50 StartY=-65 StartZ=0 EndX=-50 EndY=65 EndZ=0
  constraints (11):
    c: Coincident(g0,g1)
    c: Coincident(g1,g2)
    c: Coincident(g2,g3)
    c: Coincident(g3,g0)
    c: Horizontal(g0)
    c: Horizontal(g2)
    c: Vertical(g1)
    c: Vertical(g3)
    c: Symmetric(g0,g2,g-1)
    c: DistanceY(g1,g1) = 130
    c: DistanceX(g0,g0) = 100
FEATURE [PartDesign::Pad] Pad024
  Direction = (1,1,1)
  Length = 6
  Length2 = 100
  Placement = pos=(0,0,0) rot=(0.57735,0.57735,0.57735;2.0944rad)
  Profile = -> Sketch050
  Type = 0
FEATURE [PartDesign::Body] Body022  label="Крышка"
  Group = -> [Sketch050,Pad024]
  Origin = -> Origin050
  Placement = pos=(63,7,112) rot=(0,1,0;1.5708rad)
  Tip = -> Pad024
FEATURE [App::Part] Part004  label="Короб"
  Group = -> [Body007,Body021,mirror002,Part027,Body022]
  Origin = -> Origin032
  Placement = pos=(42,-6,-17) rot=(0,0,1;0rad)
FEATURE [App::Part] Part  label="Hand brake"
  Group = -> [Part001,Part002,Part004]
  Origin = -> Origin
FEATURE [TechDraw::DrawSVGTemplate] Template
  Height = 210
  Orientation = 1
  Width = 297
FEATURE [TechDraw::DrawProjGroupItem] ProjItem  label="Front"
  CoarseView = false
  Direction = (0,-1,0)
  Focus = 100
  HardHidden = false
  IsoCount = 0
  IsoHidden = false
  IsoVisible = false
  LockPosition = true
  Perspective = false
  Rotation = 0
  RotationVector = (1,0,0)
  Scale = 0.5
  ScaleType = 2
  SeamHidden = false
  SeamVisible = true
  SmoothHidden = false
  SmoothVisible = true
  Source = -> [Body]
  Type = 0
  X = 0
  XDirection = (1,0,0)
  Y = 0
FEATURE [TechDraw::DrawProjGroupItem] ProjItem001  label="Top"
  CoarseView = false
  Direction = (0,0,1)
  Focus = 100
  HardHidden = false
  IsoCount = 0
  IsoHidden = false
  IsoVisible = false
  LockPosition = false
  Perspective = false
  Rotation = 0
  RotationVector = (1,0,0)
  ScaleType = 2
  SeamHidden = false
  SeamVisible = true
  SmoothHidden = false
  SmoothVisible = true
  Source = -> [Body]
  Type = 4
  X = 0
  XDirection = (1,0,0)
  Y = -28.9146
FEATURE [TechDraw::DrawProjGroup] ProjGroup
  Anchor = -> ProjItem
  AutoDistribute = false
  LockPosition = false
  ProjectionType = 0
  Rotation = 0
  Scale = 0.5
  ScaleType = 2
  Source = -> [Body]
  Views = -> [ProjItem,ProjItem001]
  X = 68.9211
  Y = 182.707
  spacingX = 15
  spacingY = 15
FEATURE [TechDraw::DrawViewDimension] Dimension
  Arbitrary = false
  ArbitraryTolerances = false
  EqualTolerance = true
  FormatSpec = %.2f
  FormatSpecOverTolerance = %+.2f
  FormatSpecUnderTolerance = %+.2f
  Inverted = false
  LockPosition = false
  MeasureType = 1
  OverTolerance = 0
  References2D = -> [ProjItem]
  Rotation = 0
  ScaleType = 0
  TheoreticalExact = false
  Type = 1
  UnderTolerance = 0
  X = -1.14488
  Y = -13.7969
FEATURE [TechDraw::DrawViewDimension] Dimension001
  Arbitrary = false
  ArbitraryTolerances = false
  EqualTolerance = true
  FormatSpec = %.2f
  FormatSpecOverTolerance = %+.2f
  FormatSpecUnderTolerance = %+.2f
  Inverted = false
  LockPosition = false
  MeasureType = 1
  OverTolerance = 0
  References2D = -> [ProjItem]
  Rotation = 0
  ScaleType = 0
  TheoreticalExact = false
  Type = 2
  UnderTolerance = 0
  X = -50.6573
  Y = 0.715552
FEATURE [TechDraw::DrawViewDimension] Dimension002
  Arbitrary = false
  ArbitraryTolerances = false
  EqualTolerance = true
  FormatSpec = %.2f
  FormatSpecOverTolerance = %+.2f
  FormatSpecUnderTolerance = %+.2f
  Inverted = false
  LockPosition = false
  MeasureType = 1
  OverTolerance = 0
  References2D = -> [ProjItem]
  Rotation = 0
  ScaleType = 0
  TheoreticalExact = false
  Type = 2
  UnderTolerance = 0
  X = -40.9435
  Y = 15.4851
FEATURE [TechDraw::DrawViewDimension] Dimension003
  Arbitrary = false
  ArbitraryTolerances = false
  EqualTolerance = true
  FormatSpec = ⌀%.2f
  FormatSpecOverTolerance = %+.2f
  FormatSpecUnderTolerance = %+.2f
  Inverted = false
  LockPosition = false
  MeasureType = 1
  OverTolerance = 0
  References2D = -> [ProjItem]
  Rotation = 0
  ScaleType = 0
  TheoreticalExact = false
  Type = 5
  UnderTolerance = 0
  X = -23.6132
  Y = 5.4382
FEATURE [TechDraw::DrawViewDimension] Dimension004
  Arbitrary = false
  ArbitraryTolerances = false
  EqualTolerance = true
  FormatSpec = %.2f
  FormatSpecOverTolerance = %+.2f
  FormatSpecUnderTolerance = %+.2f
  Inverted = false
  LockPosition = false
  MeasureType = 1
  OverTolerance = 0
  References2D = -> [ProjItem]
  Rotation = 0
  ScaleType = 0
  TheoreticalExact = false
  Type = 1
  UnderTolerance = 0
  X = -26.3374
  Y = 13.8817
FEATURE [TechDraw::DrawViewDimension] Dimension005
  Arbitrary = false
  ArbitraryTolerances = false
  EqualTolerance = true
  FormatSpec = %.2f
  FormatSpecOverTolerance = %+.2f
  FormatSpecUnderTolerance = %+.2f
  Inverted = false
  LockPosition = false
  MeasureType = 1
  OverTolerance = 0
  References2D = -> [ProjItem]
  Rotation = 0
  ScaleType = 0
  TheoreticalExact = false
  Type = 1
  UnderTolerance = 0
  X = 37.0707
  Y = 15.1697
FEATURE [TechDraw::DrawViewDimension] Dimension006
  Arbitrary = false
  ArbitraryTolerances = false
  EqualTolerance = true
  FormatSpec = %.2f
  FormatSpecOverTolerance = %+.2f
  FormatSpecUnderTolerance = %+.2f
  Inverted = false
  LockPosition = false
  MeasureType = 1
  OverTolerance = 0
  References2D = -> [ProjItem]
  Rotation = 0
  ScaleType = 0
  TheoreticalExact = false
  Type = 1
  UnderTolerance = 0
  X = 26.3551
  Y = 14.7404
FEATURE [TechDraw::DrawViewDimension] Dimension007
  Arbitrary = false
  ArbitraryTolerances = false
  EqualTolerance = true
  FormatSpec = %.2f
  FormatSpecOverTolerance = %+.2f
  FormatSpecUnderTolerance = %+.2f
  Inverted = false
  LockPosition = false
  MeasureType = 1
  OverTolerance = 0
  References2D = -> [ProjItem]
  Rotation = 0
  ScaleType = 0
  TheoreticalExact = false
  Type = 2
  UnderTolerance = 0
  X = 46.4438
  Y = -0.796857
FEATURE [TechDraw::DrawViewDimension] Dimension008
  Arbitrary = false
  ArbitraryTolerances = false
  EqualTolerance = true
  FormatSpec = %.2f
  FormatSpecOverTolerance = %+.2f
  FormatSpecUnderTolerance = %+.2f
  Inverted = false
  LockPosition = false
  MeasureType = 1
  OverTolerance = 0
  References2D = -> [ProjItem]
  Rotation = 0
  ScaleType = 0
  TheoreticalExact = false
  Type = 1
  UnderTolerance = 0
  X = 25.4293
  Y = -8.66438
FEATURE [TechDraw::DrawViewDimension] Dimension009
  Arbitrary = false
  ArbitraryTolerances = false
  EqualTolerance = true
  FormatSpec = %.2f
  FormatSpecOverTolerance = %+.2f
  FormatSpecUnderTolerance = %+.2f
  Inverted = false
  LockPosition = false
  MeasureType = 1
  OverTolerance = 0
  References2D = -> [ProjItem]
  Rotation = 0
  ScaleType = 0
  TheoreticalExact = false
  Type = 1
  UnderTolerance = 0
  X = 2.07067
  Y = -0.507091
FEATURE [TechDraw::DrawViewDimension] Dimension010
  Arbitrary = false
  ArbitraryTolerances = false
  EqualTolerance = true
  FormatSpec = %.2f
  FormatSpecOverTolerance = %+.2f
  FormatSpecUnderTolerance = %+.2f
  Inverted = false
  LockPosition = false
  MeasureType = 1
  OverTolerance = 0
  References2D = -> [ProjItem]
  Rotation = 0
  ScaleType = 0
  TheoreticalExact = false
  Type = 1
  UnderTolerance = 0
  X = -23.2156
  Y = -7.23328
FEATURE [TechDraw::DrawViewDimension] Dimension011
  Arbitrary = false
  ArbitraryTolerances = false
  EqualTolerance = true
  FormatSpec = %.2f
  FormatSpecOverTolerance = %+.2f
  FormatSpecUnderTolerance = %+.2f
  Inverted = false
  LockPosition = false
  MeasureType = 1
  OverTolerance = 0
  References2D = -> [ProjItem001]
  Rotation = 0
  ScaleType = 0
  TheoreticalExact = false
  Type = 1
  UnderTolerance = 0
  X = 29.5529
  Y = -8.15729
FEATURE [TechDraw::DrawViewDimension] Dimension012
  Arbitrary = false
  ArbitraryTolerances = false
  EqualTolerance = true
  FormatSpec = %.2f
  FormatSpecOverTolerance = %+.2f
  FormatSpecUnderTolerance = %+.2f
  Inverted = false
  LockPosition = false
  MeasureType = 1
  OverTolerance = 0
  References2D = -> [ProjItem001]
  Rotation = 0
  ScaleType = 0
  TheoreticalExact = false
  Type = 1
  UnderTolerance = 0
  X = -29.1236
  Y = -9.87462
FEATURE [TechDraw::DrawProjGroupItem] ProjItem002  label="Front001"
  CoarseView = false
  Direction = (0,-1,0)
  Focus = 100
  HardHidden = false
  IsoCount = 0
  IsoHidden = false
  IsoVisible = false
  LockPosition = true
  Perspective = false
  Rotation = 0
  RotationVector = (1,0,0)
  Scale = 0.5
  ScaleType = 2
  SeamHidden = false
  SeamVisible = true
  SmoothHidden = false
  SmoothVisible = true
  Source = -> [Body003]
  Type = 0
  X = 0
  XDirection = (1,0,0)
  Y = 0
FEATURE [TechDraw::DrawProjGroup] ProjGroup001
  Anchor = -> ProjItem002
  AutoDistribute = true
  LockPosition = false
  ProjectionType = 0
  Rotation = 0
  Scale = 0.5
  ScaleType = 2
  Source = -> [Body003]
  Views = -> [ProjItem002]
  X = 253.435
  Y = 162.344
  spacingX = 15
  spacingY = 15
FEATURE [TechDraw::DrawProjGroupItem] ProjItem003  label="Front002"
  CoarseView = false
  Direction = (0,-1,0)
  Focus = 100
  HardHidden = false
  IsoCount = 0
  IsoHidden = false
  IsoVisible = false
  LockPosition = true
  Perspective = false
  Rotation = 0
  RotationVector = (1,0,0)
  Scale = 0.5
  ScaleType = 2
  SeamHidden = false
  SeamVisible = true
  SmoothHidden = false
  SmoothVisible = true
  Source = -> [Body002]
  Type = 0
  X = 0
  XDirection = (1,0,0)
  Y = 0
FEATURE [TechDraw::DrawProjGroup] ProjGroup002
  Anchor = -> ProjItem003
  AutoDistribute = true
  LockPosition = false
  ProjectionType = 0
  Rotation = 0
  Scale = 0.5
  ScaleType = 2
  Source = -> [Body002]
  Views = -> [ProjItem003]
  X = 194.824
  Y = 161.618
  spacingX = 15
  spacingY = 15
FEATURE [TechDraw::DrawViewDimension] Dimension013
  Arbitrary = false
  ArbitraryTolerances = false
  EqualTolerance = true
  FormatSpec = %.2f
  FormatSpecOverTolerance = %+.2f
  FormatSpecUnderTolerance = %+.2f
  Inverted = false
  LockPosition = false
  MeasureType = 1
  OverTolerance = 0
  References2D = -> [ProjItem003]
  Rotation = 0
  ScaleType = 0
  TheoreticalExact = false
  Type = 2
  UnderTolerance = 0
  X = 19.1591
  Y = 0
FEATURE [TechDraw::DrawViewDimension] Dimension014
  Arbitrary = false
  ArbitraryTolerances = false
  EqualTolerance = true
  FormatSpec = %.2f
  FormatSpecOverTolerance = %+.2f
  FormatSpecUnderTolerance = %+.2f
  Inverted = false
  LockPosition = false
  MeasureType = 1
  OverTolerance = 0
  References2D = -> [ProjItem002]
  Rotation = 0
  ScaleType = 0
  TheoreticalExact = false
  Type = 2
  UnderTolerance = 0
  X = 18.5866
  Y = 0
FEATURE [TechDraw::DrawViewDimension] Dimension015
  Arbitrary = false
  ArbitraryTolerances = false
  EqualTolerance = true
  FormatSpec = %.2f
  FormatSpecOverTolerance = %+.2f
  FormatSpecUnderTolerance = %+.2f
  Inverted = false
  LockPosition = false
  MeasureType = 1
  OverTolerance = 0
  References2D = -> [ProjItem002]
  Rotation = 0
  ScaleType = 0
  TheoreticalExact = false
  Type = 1
  UnderTolerance = 0
  X = 2.7191
  Y = -25.4471
FEATURE [TechDraw::DrawViewDimension] Dimension016
  Arbitrary = false
  ArbitraryTolerances = false
  EqualTolerance = true
  FormatSpec = %.2f
  FormatSpecOverTolerance = %+.2f
  FormatSpecUnderTolerance = %+.2f
  Inverted = false
  LockPosition = false
  MeasureType = 1
  OverTolerance = 0
  References2D = -> [ProjItem003]
  Rotation = 0
  ScaleType = 0
  TheoreticalExact = false
  Type = 1
  UnderTolerance = 0
  X = 0.429331
  Y = 29.4453
FEATURE [TechDraw::DrawProjGroupItem] ProjItem004  label="Front003"
  CoarseView = false
  Direction = (-1,0,0)
  Focus = 100
  HardHidden = false
  IsoCount = 0
  IsoHidden = false
  IsoVisible = false
  LockPosition = true
  Perspective = false
  Rotation = 0
  RotationVector = (0,-1,0)
  Scale = 0.5
  ScaleType = 2
  SeamHidden = false
  SeamVisible = true
  SmoothHidden = false
  SmoothVisible = true
  Source = -> [Pocket]
  Type = 0
  X = 0
  XDirection = (0,-1e-16,-1)
  Y = 0
FEATURE [TechDraw::DrawProjGroupItem] ProjItem006  label="Top001"
  CoarseView = false
  Direction = (0,-1,1e-16)
  Focus = 100
  HardHidden = false
  IsoCount = 0
  IsoHidden = false
  IsoVisible = false
  LockPosition = false
  Perspective = false
  Rotation = 0
  RotationVector = (1,0,0)
  Scale = 0.5
  ScaleType = 2
  SeamHidden = false
  SeamVisible = true
  SmoothHidden = false
  SmoothVisible = true
  Source = -> [Pocket]
  Type = 4
  X = 0
  XDirection = (0,-1e-16,-1)
  Y = -28.5116
FEATURE [TechDraw::DrawProjGroup] ProjGroup003
  Anchor = -> ProjItem004
  AutoDistribute = true
  LockPosition = false
  ProjectionType = 0
  Rotation = 0
  Scale = 0.5
  ScaleType = 2
  Source = -> [Pocket]
  Views = -> [ProjItem004,ProjItem006]
  X = 66.1124
  Y = 90.4885
  spacingX = 15
  spacingY = 15
FEATURE [TechDraw::DrawViewDimension] Dimension017
  Arbitrary = false
  ArbitraryTolerances = false
  EqualTolerance = true
  FormatSpec = %.2f
  FormatSpecOverTolerance = %+.2f
  FormatSpecUnderTolerance = %+.2f
  Inverted = false
  LockPosition = false
  MeasureType = 1
  OverTolerance = 0
  References2D = -> [ProjItem006]
  Rotation = 0
  ScaleType = 0
  TheoreticalExact = false
  Type = 1
  UnderTolerance = 0
  X = -0.451496
  Y = 17.3602
FEATURE [TechDraw::DrawViewDimension] Dimension018
  Arbitrary = false
  ArbitraryTolerances = false
  EqualTolerance = true
  FormatSpec = %.2f
  FormatSpecOverTolerance = %+.2f
  FormatSpecUnderTolerance = %+.2f
  Inverted = false
  LockPosition = false
  MeasureType = 1
  OverTolerance = 0
  References2D = -> [ProjItem006]
  Rotation = 0
  ScaleType = 0
  TheoreticalExact = false
  Type = 1
  UnderTolerance = 0
  X = 39.3604
  Y = -15.0266
FEATURE [TechDraw::DrawViewDimension] Dimension019
  Arbitrary = false
  ArbitraryTolerances = false
  EqualTolerance = true
  FormatSpec = %.2f
  FormatSpecOverTolerance = %+.2f
  FormatSpecUnderTolerance = %+.2f
  Inverted = false
  LockPosition = false
  MeasureType = 1
  OverTolerance = 0
  References2D = -> [ProjItem006]
  Rotation = 0
  ScaleType = 0
  TheoreticalExact = false
  Type = 1
  UnderTolerance = 0
  X = 29.7138
  Y = -8.44351
FEATURE [TechDraw::DrawProjGroupItem] ProjItem007  label="Front004"
  CoarseView = false
  Direction = (0,-1,0)
  Focus = 100
  HardHidden = false
  IsoCount = 0
  IsoHidden = false
  IsoVisible = false
  LockPosition = true
  Perspective = false
  Rotation = 0
  RotationVector = (1,0,0)
  ScaleType = 2
  SeamHidden = false
  SeamVisible = true
  SmoothHidden = false
  SmoothVisible = true
  Source = -> [Body004]
  Type = 0
  X = 0
  XDirection = (1,0,0)
  Y = 0
FEATURE [TechDraw::DrawProjGroup] ProjGroup004
  Anchor = -> ProjItem007
  AutoDistribute = true
  LockPosition = false
  ProjectionType = 0
  Rotation = 0
  ScaleType = 0
  Source = -> [Body004]
  Views = -> [ProjItem007]
  X = 166.379
  Y = 65.4489
  spacingX = 15
  spacingY = 15
FEATURE [TechDraw::DrawViewDimension] Dimension020
  Arbitrary = false
  ArbitraryTolerances = false
  EqualTolerance = true
  FormatSpec = %.2f
  FormatSpecOverTolerance = %+.2f
  FormatSpecUnderTolerance = %+.2f
  Inverted = false
  LockPosition = false
  MeasureType = 1
  OverTolerance = 0
  References2D = -> [ProjItem007]
  Rotation = 0
  ScaleType = 0
  TheoreticalExact = false
  Type = 1
  UnderTolerance = 0
  X = 1.62539
  Y = 23.3158
FEATURE [TechDraw::DrawViewDimension] Dimension021
  Arbitrary = false
  ArbitraryTolerances = false
  EqualTolerance = true
  FormatSpec = %.2f
  FormatSpecOverTolerance = %+.2f
  FormatSpecUnderTolerance = %+.2f
  Inverted = false
  LockPosition = false
  MeasureType = 1
  OverTolerance = 0
  References2D = -> [ProjItem007]
  Rotation = 0
  ScaleType = 0
  TheoreticalExact = false
  Type = 1
  UnderTolerance = 0
  X = 32.709
  Y = -21.9427
FEATURE [TechDraw::DrawSVGTemplate] Template001
  Height = 210
  Orientation = 1
  Width = 297
FEATURE [TechDraw::DrawProjGroupItem] ProjItem008  label="Front005"
  CoarseView = false
  Direction = (0,0,1)
  Focus = 100
  HardHidden = false
  IsoCount = 0
  IsoHidden = false
  IsoVisible = false
  LockPosition = true
  Perspective = false
  Rotation = 0
  RotationVector = (1,0,0)
  Scale = 0.5
  ScaleType = 2
  SeamHidden = false
  SeamVisible = true
  SmoothHidden = false
  SmoothVisible = true
  Source = -> [Body007]
  Type = 0
  X = 0
  XDirection = (1,0,0)
  Y = 0
FEATURE [TechDraw::DrawProjGroup] ProjGroup005
  Anchor = -> ProjItem008
  AutoDistribute = true
  LockPosition = false
  ProjectionType = 0
  Rotation = 0
  Scale = 0.5
  ScaleType = 2
  Source = -> [Body007]
  Views = -> [ProjItem008]
  X = 66.8809
  Y = 162.262
  spacingX = 15
  spacingY = 15
FEATURE [TechDraw::DrawViewDimension] Dimension022
  Arbitrary = false
  ArbitraryTolerances = false
  EqualTolerance = true
  FormatSpec = %.2f
  FormatSpecOverTolerance = %+.2f
  FormatSpecUnderTolerance = %+.2f
  Inverted = false
  LockPosition = false
  MeasureType = 1
  OverTolerance = 0
  References2D = -> [ProjItem008]
  Rotation = 0
  ScaleType = 0
  TheoreticalExact = false
  Type = 1
  UnderTolerance = 0
  X = -0.427325
  Y = 36.9651
FEATURE [TechDraw::DrawViewDimension] Dimension023
  Arbitrary = false
  ArbitraryTolerances = false
  EqualTolerance = true
  FormatSpec = %.2f
  FormatSpecOverTolerance = %+.2f
  FormatSpecUnderTolerance = %+.2f
  Inverted = false
  LockPosition = false
  MeasureType = 1
  OverTolerance = 0
  References2D = -> [ProjItem008]
  Rotation = 0
  ScaleType = 0
  TheoreticalExact = false
  Type = 2
  UnderTolerance = 0
  X = 51.4738
  Y = 0.427325
FEATURE [TechDraw::DrawProjGroupItem] ProjItem009  label="Front006"
  CoarseView = false
  Direction = (0,-1,0)
  Focus = 100
  HardHidden = false
  IsoCount = 0
  IsoHidden = false
  IsoVisible = false
  LockPosition = true
  Perspective = false
  Rotation = 0
  RotationVector = (1,0,0)
  ScaleType = 2
  SeamHidden = false
  SeamVisible = true
  SmoothHidden = false
  SmoothVisible = true
  Source = -> [Body005]
  Type = 0
  X = 0
  XDirection = (1,0,0)
  Y = 0
FEATURE [TechDraw::DrawProjGroupItem] ProjItem010  label="Bottom"
  CoarseView = false
  Direction = (0,0,-1)
  Focus = 100
  HardHidden = false
  IsoCount = 0
  IsoHidden = false
  IsoVisible = false
  LockPosition = false
  Perspective = false
  Rotation = 0
  RotationVector = (1,0,0)
  ScaleType = 2
  SeamHidden = false
  SeamVisible = true
  SmoothHidden = false
  SmoothVisible = true
  Source = -> [Body005]
  Type = 5
  X = 0
  XDirection = (1,0,0)
  Y = -21.8235
FEATURE [TechDraw::DrawProjGroup] ProjGroup006
  Anchor = -> ProjItem009
  AutoDistribute = false
  LockPosition = false
  ProjectionType = 0
  Rotation = 0
  ScaleType = 0
  Source = -> [Body005]
  Views = -> [ProjItem009,ProjItem010]
  X = 245.471
  Y = 82.4559
  spacingX = 15
  spacingY = 15
FEATURE [TechDraw::DrawViewDimension] Dimension024
  Arbitrary = false
  ArbitraryTolerances = false
  EqualTolerance = true
  FormatSpec = %.2f
  FormatSpecOverTolerance = %+.2f
  FormatSpecUnderTolerance = %+.2f
  Inverted = false
  LockPosition = false
  MeasureType = 1
  OverTolerance = 0
  References2D = -> [ProjItem010]
  Rotation = 0
  ScaleType = 0
  TheoreticalExact = false
  Type = 1
  UnderTolerance = 0
  X = 0.617647
  Y = -18
FEATURE [TechDraw::DrawViewDimension] Dimension025
  Arbitrary = false
  ArbitraryTolerances = false
  EqualTolerance = true
  FormatSpec = %.2f
  FormatSpecOverTolerance = %+.2f
  FormatSpecUnderTolerance = %+.2f
  Inverted = false
  LockPosition = false
  MeasureType = 1
  OverTolerance = 0
  References2D = -> [ProjItem010]
  Rotation = 0
  ScaleType = 0
  TheoreticalExact = false
  Type = 2
  UnderTolerance = 0
  X = -20.8382
  Y = 0
FEATURE [TechDraw::DrawViewDimension] Dimension026
  Arbitrary = false
  ArbitraryTolerances = false
  EqualTolerance = true
  FormatSpec = %.2f
  FormatSpecOverTolerance = %+.2f
  FormatSpecUnderTolerance = %+.2f
  Inverted = false
  LockPosition = false
  MeasureType = 1
  OverTolerance = 0
  References2D = -> [ProjItem010]
  Rotation = 0
  ScaleType = 0
  TheoreticalExact = false
  Type = 1
  UnderTolerance = 0
  X = -10.6176
  Y = -31.1912
FEATURE [TechDraw::DrawViewDimension] Dimension027
  Arbitrary = false
  ArbitraryTolerances = false
  EqualTolerance = true
  FormatSpec = %.2f
  FormatSpecOverTolerance = %+.2f
  FormatSpecUnderTolerance = %+.2f
  Inverted = false
  LockPosition = false
  MeasureType = 1
  OverTolerance = 0
  References2D = -> [ProjItem010]
  Rotation = 0
  ScaleType = 0
  TheoreticalExact = false
  Type = 1
  UnderTolerance = 0
  X = 9.38235
  Y = -33.6618
FEATURE [TechDraw::DrawViewDimension] Dimension028
  Arbitrary = false
  ArbitraryTolerances = false
  EqualTolerance = true
  FormatSpec = ⌀%.2f
  FormatSpecOverTolerance = %+.2f
  FormatSpecUnderTolerance = %+.2f
  Inverted = false
  LockPosition = false
  MeasureType = 1
  OverTolerance = 0
  References2D = -> [ProjItem010]
  Rotation = 0
  ScaleType = 0
  TheoreticalExact = false
  Type = 5
  UnderTolerance = 0
  X = 27.1765
  Y = 4.01471
FEATURE [TechDraw::DrawViewDimension] Dimension029
  Arbitrary = false
  ArbitraryTolerances = false
  EqualTolerance = true
  FormatSpec = ⌀%.2f
  FormatSpecOverTolerance = %+.2f
  FormatSpecUnderTolerance = %+.2f
  Inverted = false
  LockPosition = false
  MeasureType = 1
  OverTolerance = 0
  References2D = -> [ProjItem010]
  Rotation = 0
  ScaleType = 0
  TheoreticalExact = false
  Type = 5
  UnderTolerance = 0
  X = -26.5588
  Y = -13.5882
FEATURE [TechDraw::DrawPage] Page  label="Основа"
  KeepUpdated = true
  NextBalloonIndex = 1
  ProjectionType = 0
  Template = -> Template
  Views = -> [ProjGroup,Dimension,Dimension001,Dimension002,Dimension003,Dimension004,Dimension005,Dimension006,Dimension007,Dimension008,Dimension009,Dimension010,Dimension011,Dimension012,ProjGroup001,ProjGroup002,Dimension013,Dimension014,Dimension015,Dimension016,ProjGroup003,Dimension017,Dimension018,Dimension019,ProjGroup004,Dimension020,Dimension021,ProjGroup006,Dimension024,Dimension025,Dimension026,+3 more]
FEATURE [TechDraw::DrawProjGroupItem] ProjItem011  label="Front007"
  CoarseView = false
  Direction = (0,-1,0)
  Focus = 100
  HardHidden = false
  IsoCount = 0
  IsoHidden = false
  IsoVisible = false
  LockPosition = true
  Perspective = false
  Rotation = 0
  RotationVector = (1,0,0)
  Scale = 0.5
  ScaleType = 2
  SeamHidden = false
  SeamVisible = true
  SmoothHidden = false
  SmoothVisible = true
  Source = -> [Body021]
  Type = 0
  X = 0
  XDirection = (1e-16,0,1)
  Y = 0
FEATURE [TechDraw::DrawProjGroup] ProjGroup007
  Anchor = -> ProjItem011
  AutoDistribute = true
  LockPosition = false
  ProjectionType = 0
  Rotation = 0
  Scale = 0.5
  ScaleType = 2
  Source = -> [Body021]
  Views = -> [ProjItem011]
  X = 49.9853
  Y = 59.6029
  spacingX = 15
  spacingY = 15
FEATURE [TechDraw::DrawProjGroupItem] ProjItem012  label="Front008"
  CoarseView = false
  Direction = (0,0,1)
  Focus = 100
  HardHidden = false
  IsoCount = 0
  IsoHidden = false
  IsoVisible = false
  LockPosition = true
  Perspective = false
  Rotation = 0
  RotationVector = (1,0,0)
  Scale = 0.5
  ScaleType = 2
  SeamHidden = false
  SeamVisible = true
  SmoothHidden = false
  SmoothVisible = true
  Source = -> [Body022]
  Type = 0
  X = 0
  XDirection = (1,0,0)
  Y = 0
FEATURE [TechDraw::DrawProjGroup] ProjGroup008
  Anchor = -> ProjItem012
  AutoDistribute = true
  LockPosition = false
  ProjectionType = 0
  Rotation = 0
  Scale = 0.5
  ScaleType = 2
  Source = -> [Body022]
  Views = -> [ProjItem012]
  X = 137.691
  Y = 45.3971
  spacingX = 15
  spacingY = 15
FEATURE [TechDraw::DrawViewDimension] Dimension030
  Arbitrary = false
  ArbitraryTolerances = false
  EqualTolerance = true
  FormatSpec = %.2f
  FormatSpecOverTolerance = %+.2f
  FormatSpecUnderTolerance = %+.2f
  Inverted = false
  LockPosition = false
  MeasureType = 1
  OverTolerance = 0
  References2D = -> [ProjItem011]
  Rotation = 0
  ScaleType = 0
  TheoreticalExact = false
  Type = 1
  UnderTolerance = 0
  X = -0.845748
  Y = -48.7022
FEATURE [TechDraw::DrawViewDimension] Dimension031
  Arbitrary = false
  ArbitraryTolerances = false
  EqualTolerance = true
  FormatSpec = %.2f
  FormatSpecOverTolerance = %+.2f
  FormatSpecUnderTolerance = %+.2f
  Inverted = false
  LockPosition = false
  MeasureType = 1
  OverTolerance = 0
  References2D = -> [ProjItem011]
  Rotation = 0
  ScaleType = 0
  TheoreticalExact = false
  Type = 2
  UnderTolerance = 0
  X = -33.4947
  Y = 1.6915
FEATURE [TechDraw::DrawViewDimension] Dimension032
  Arbitrary = false
  ArbitraryTolerances = false
  EqualTolerance = true
  FormatSpec = %.2f
  FormatSpecOverTolerance = %+.2f
  FormatSpecUnderTolerance = %+.2f
  Inverted = false
  LockPosition = false
  MeasureType = 1
  OverTolerance = 0
  References2D = -> [ProjItem011]
  Rotation = 0
  ScaleType = 0
  TheoreticalExact = false
  Type = 1
  UnderTolerance = 0
  X = -7.5
  Y = 53.4947
FEATURE [TechDraw::DrawViewDimension] Dimension033
  Arbitrary = false
  ArbitraryTolerances = false
  EqualTolerance = true
  FormatSpec = %.2f
  FormatSpecOverTolerance = %+.2f
  FormatSpecUnderTolerance = %+.2f
  Inverted = false
  LockPosition = false
  MeasureType = 1
  OverTolerance = 0
  References2D = -> [ProjItem011]
  Rotation = 0
  ScaleType = 0
  TheoreticalExact = false
  Type = 2
  UnderTolerance = 0
  X = 29.8298
  Y = -11.4096
FEATURE [TechDraw::DrawViewDimension] Dimension034
  Arbitrary = false
  ArbitraryTolerances = false
  EqualTolerance = true
  FormatSpec = %.2f
  FormatSpecOverTolerance = %+.2f
  FormatSpecUnderTolerance = %+.2f
  Inverted = false
  LockPosition = false
  MeasureType = 1
  OverTolerance = 0
  References2D = -> [ProjItem012]
  Rotation = 0
  ScaleType = 0
  TheoreticalExact = false
  Type = 2
  UnderTolerance = 0
  X = -46.032
  Y = 1.97341
FEATURE [TechDraw::DrawViewDimension] Dimension035
  Arbitrary = false
  ArbitraryTolerances = false
  EqualTolerance = true
  FormatSpec = %.2f
  FormatSpecOverTolerance = %+.2f
  FormatSpecUnderTolerance = %+.2f
  Inverted = false
  LockPosition = false
  MeasureType = 1
  OverTolerance = 0
  References2D = -> [ProjItem012]
  Rotation = 0
  ScaleType = 0
  TheoreticalExact = false
  Type = 1
  UnderTolerance = 0
  X = -0.281916
  Y = 38.532
FEATURE [TechDraw::DrawPage] Page001  label="Короб001"
  KeepUpdated = true
  NextBalloonIndex = 1
  ProjectionType = 0
  Template = -> Template001
  Views = -> [ProjGroup005,Dimension022,Dimension023,ProjGroup007,ProjGroup008,Dimension030,Dimension031,Dimension032,Dimension033,Dimension034,Dimension035]
FEATURE [App::DocumentObjectGroup] Group  label="Чертежи"
  Group = -> [Page,Page001]
